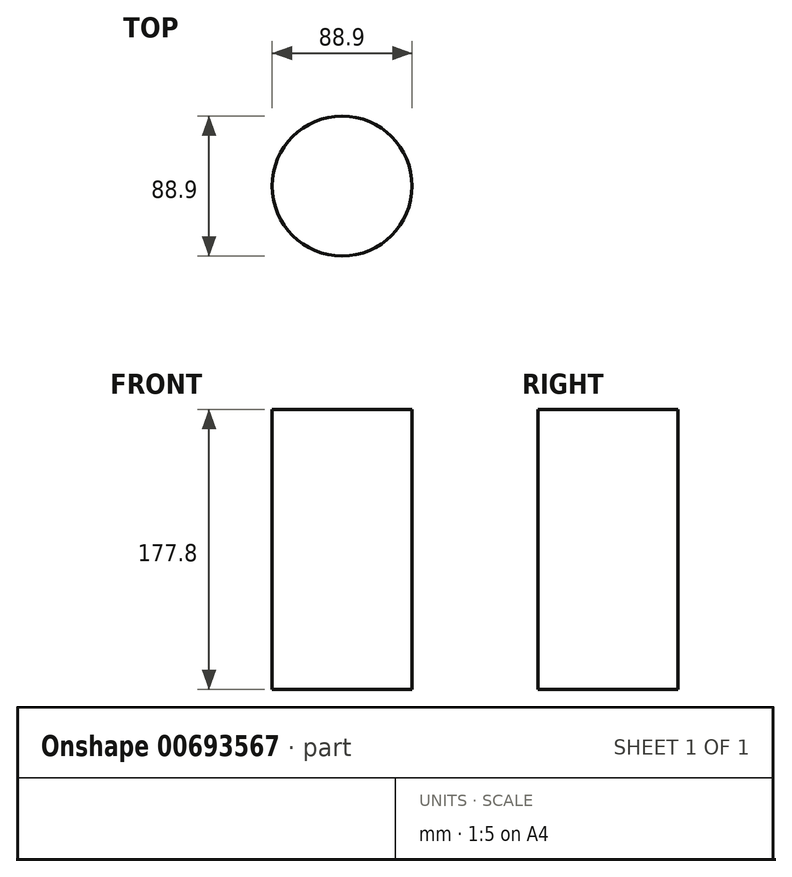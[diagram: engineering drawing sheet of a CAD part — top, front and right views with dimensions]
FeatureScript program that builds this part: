
annotation { "Feature Type Name" : "Feature", "Feature Type Description" : "" }
export const myFeature = defineFeature(function(context is Context, id is Id, definition is map)
    precondition{}
    {
        {
            var Q0;
            Q0=qCreatedBy(makeId("Top.planeOp"),FACE);
            var sketch = newSketch(context, id + "F0", { "sketchPlane" : qUnion([Q0])});
            skCircle(sketch, "E0", {"center": v(0, 0) * mm, "radius": 44.45 * mm});
            skSolve(sketch);
        }
        {
            var Q0;
            Q0 = qSketchRegion(id + "F0", true);
            extrude(context, id + "F1", {"entities" : qUnion([Q0]), "oppositeDirection" : true, "depth" : 177.8 * mm, "offsetDistance" : 25 * mm});
        }
    });
